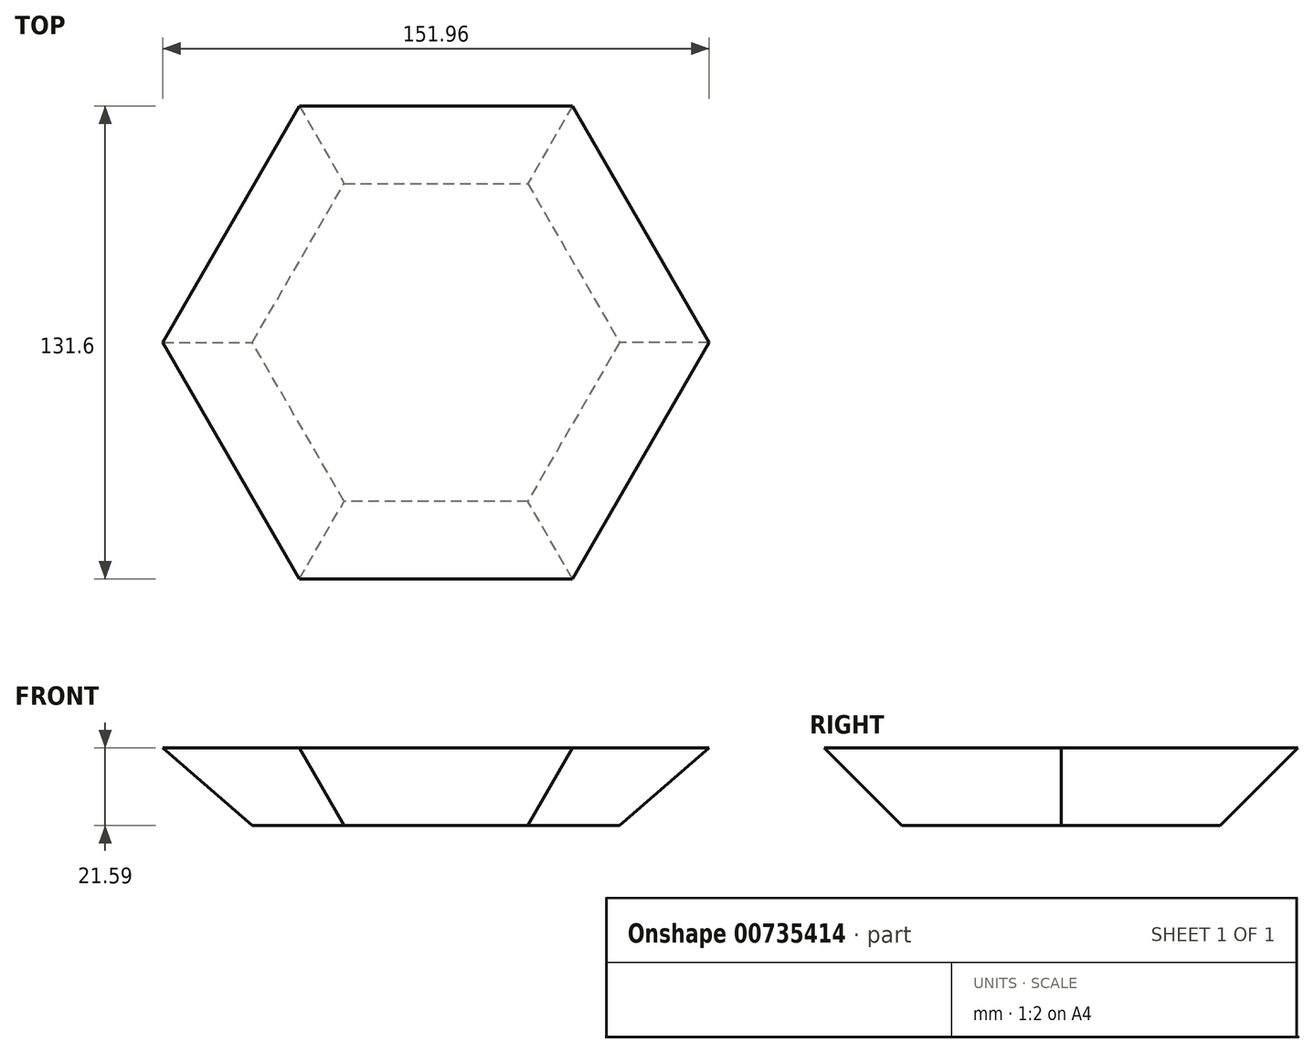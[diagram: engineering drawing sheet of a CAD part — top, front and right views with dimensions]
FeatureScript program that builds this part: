
annotation { "Feature Type Name" : "Feature", "Feature Type Description" : "" }
export const myFeature = defineFeature(function(context is Context, id is Id, definition is map)
    precondition{}
    {
        {
            var Q0;
            Q0=qCreatedBy(makeId("Top.planeOp"),FACE);
            var sketch = newSketch(context, id + "F0", { "sketchPlane" : qUnion([Q0])});
            skCircle(sketch, "E0.cCircle", {"center": v(0, 0) * mm, "radius": 51.05 * mm, "construction": true});
            skLineSegment(sketch, "E0.0", {"start": v(-51.05, 0) * mm, "end": v(-25.52, 44.2) * mm});
            skLineSegment(sketch, "E0.1", {"start": v(-25.52, 44.2) * mm, "end": v(25.52, 44.2) * mm});
            skLineSegment(sketch, "E0.2", {"start": v(25.52, 44.2) * mm, "end": v(51.05, 0) * mm});
            skLineSegment(sketch, "E0.3", {"start": v(51.05, 0) * mm, "end": v(25.52, -44.2) * mm});
            skLineSegment(sketch, "E0.4", {"start": v(25.52, -44.2) * mm, "end": v(-25.52, -44.2) * mm});
            skLineSegment(sketch, "E0.5", {"start": v(-25.52, -44.2) * mm, "end": v(-51.05, 0) * mm});
            skSolve(sketch);
        }
        {
            var Q0;
            Q0=makeQuery(id+"F0.imprint","IMPRINT",FACE,{"disambiguationData":[TD([[makeQuery(id+"F0.imprint","IMPRINT",EDGE,{"derivedFrom":sQuery(id+"F0.wireOp",EDGE,"E0.0")}),-1.0]])]});
            extrude(context, id + "F1", {"entities" : qUnion([Q0]), "depth" : 21.59 * mm, "offsetDistance" : 25.4 * mm, "hasDraft" : true, "draftAngle" : 45 * degree});
        }
    });
